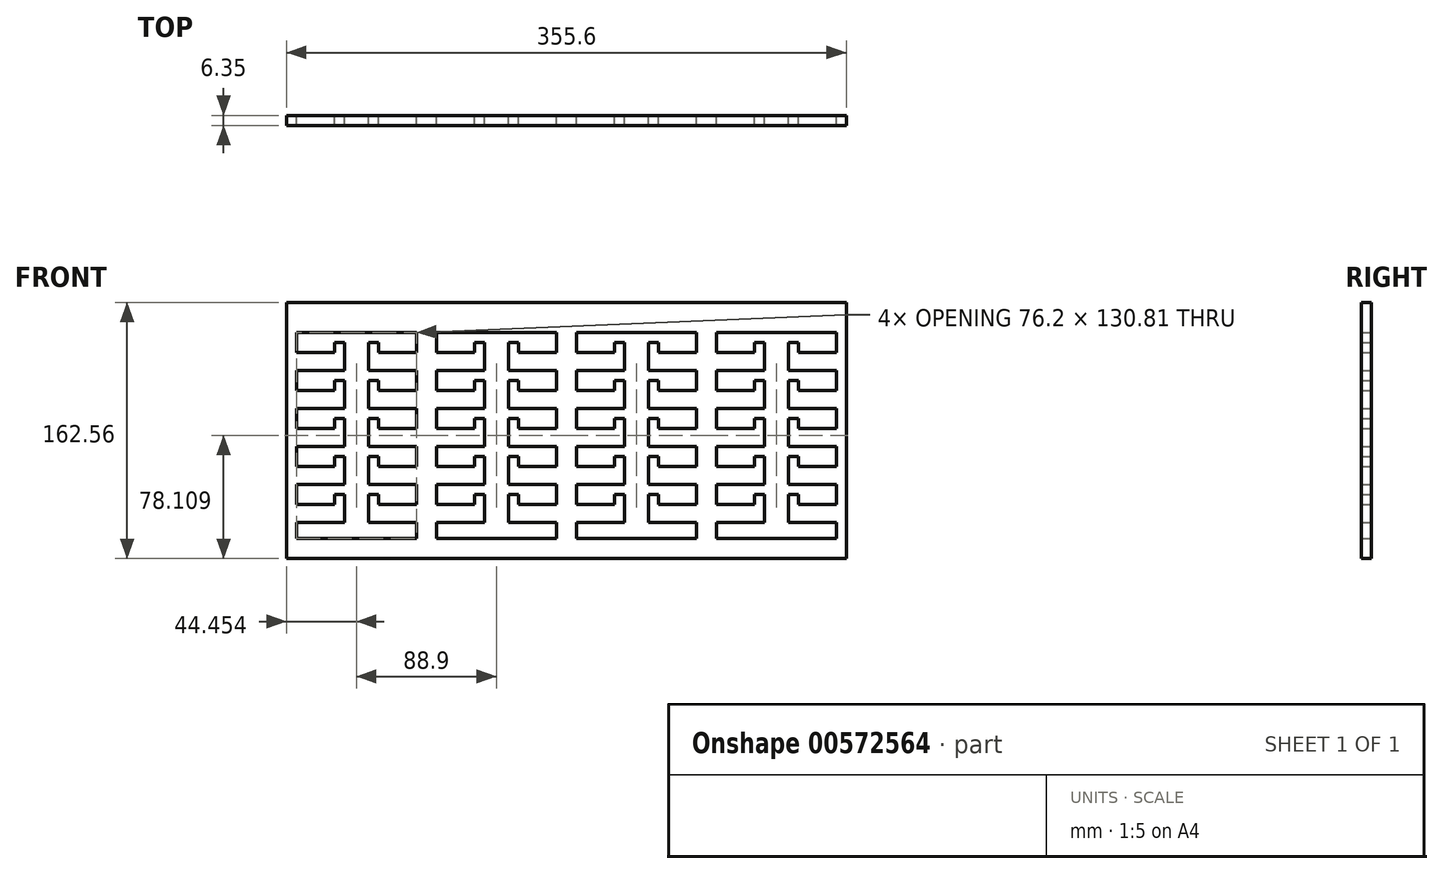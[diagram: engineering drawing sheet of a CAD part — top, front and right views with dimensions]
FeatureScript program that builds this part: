
annotation { "Feature Type Name" : "Feature", "Feature Type Description" : "" }
export const myFeature = defineFeature(function(context is Context, id is Id, definition is map)
    precondition{}
    {
        {
            var Q0;
            Q0=qCreatedBy(makeId("Front.planeOp"),FACE);
            var sketch = newSketch(context, id + "F0", { "sketchPlane" : qUnion([Q0])});
            skLineSegment(sketch, "E0", {"start": v(-96.23, -25.4) * mm, "end": v(-65.75, -25.4) * mm});
            skLineSegment(sketch, "E1", {"start": v(-65.75, -25.4) * mm, "end": v(-65.75, -7.62) * mm});
            skLineSegment(sketch, "E2", {"start": v(-65.75, -7.62) * mm, "end": v(-72.1, -7.62) * mm});
            skLineSegment(sketch, "E3", {"start": v(-72.1, -7.62) * mm, "end": v(-72.1, -13.97) * mm});
            skLineSegment(sketch, "E4", {"start": v(-72.1, -13.97) * mm, "end": v(-96.23, -13.97) * mm});
            skLineSegment(sketch, "E5", {"start": v(-96.23, -13.97) * mm, "end": v(-96.23, -1.27) * mm});
            skLineSegment(sketch, "E6", {"start": v(-96.23, -1.27) * mm, "end": v(-65.75, -1.27) * mm});
            skLineSegment(sketch, "E7", {"start": v(-65.75, -1.27) * mm, "end": v(-65.75, 16.51) * mm});
            skLineSegment(sketch, "E8", {"start": v(-65.75, 16.51) * mm, "end": v(-72.1, 16.51) * mm});
            skLineSegment(sketch, "E9", {"start": v(-72.1, 16.51) * mm, "end": v(-72.1, 10.16) * mm});
            skLineSegment(sketch, "E10", {"start": v(-72.1, 10.16) * mm, "end": v(-96.23, 10.16) * mm});
            skLineSegment(sketch, "E11", {"start": v(-96.23, 10.16) * mm, "end": v(-96.23, 22.86) * mm});
            skLineSegment(sketch, "E12", {"start": v(-96.23, 22.86) * mm, "end": v(-65.75, 22.86) * mm});
            skLineSegment(sketch, "E13", {"start": v(-65.75, 22.86) * mm, "end": v(-65.75, 40.64) * mm});
            skLineSegment(sketch, "E14", {"start": v(-65.75, 40.64) * mm, "end": v(-72.1, 40.64) * mm});
            skLineSegment(sketch, "E15", {"start": v(-72.1, 40.64) * mm, "end": v(-72.1, 34.3) * mm});
            skLineSegment(sketch, "E16", {"start": v(-72.1, 34.3) * mm, "end": v(-96.23, 34.3) * mm});
            skLineSegment(sketch, "E17", {"start": v(-96.23, 34.3) * mm, "end": v(-96.23, 47) * mm});
            skLineSegment(sketch, "E18", {"start": v(-96.23, 47) * mm, "end": v(-65.75, 47) * mm});
            skLineSegment(sketch, "E19", {"start": v(-65.75, 64.77) * mm, "end": v(-72.1, 64.77) * mm});
            skLineSegment(sketch, "E20", {"start": v(-72.1, 64.77) * mm, "end": v(-72.1, 58.42) * mm});
            skLineSegment(sketch, "E21", {"start": v(-72.1, 58.42) * mm, "end": v(-96.23, 58.42) * mm});
            skLineSegment(sketch, "E22", {"start": v(-96.23, 58.42) * mm, "end": v(-96.23, 71.12) * mm});
            skLineSegment(sketch, "E23", {"start": v(-20.03, -59.69) * mm, "end": v(-20.03, -49.53) * mm});
            skLineSegment(sketch, "E24", {"start": v(-20.03, -49.53) * mm, "end": v(-50.5, -49.53) * mm});
            skLineSegment(sketch, "E25", {"start": v(-50.5, -49.53) * mm, "end": v(-50.5, -31.75) * mm});
            skLineSegment(sketch, "E26", {"start": v(-50.5, -31.75) * mm, "end": v(-44.16, -31.75) * mm});
            skLineSegment(sketch, "E27", {"start": v(-44.16, -31.75) * mm, "end": v(-44.16, -38.1) * mm});
            skLineSegment(sketch, "E28", {"start": v(-44.16, -38.1) * mm, "end": v(-20.03, -38.1) * mm});
            skLineSegment(sketch, "E29", {"start": v(-20.03, -38.1) * mm, "end": v(-20.03, -25.4) * mm});
            skLineSegment(sketch, "E30", {"start": v(-20.03, -25.4) * mm, "end": v(-50.5, -25.4) * mm});
            skLineSegment(sketch, "E31", {"start": v(-50.5, -25.4) * mm, "end": v(-50.5, -7.62) * mm});
            skLineSegment(sketch, "E32", {"start": v(-50.5, -7.62) * mm, "end": v(-44.16, -7.62) * mm});
            skLineSegment(sketch, "E33", {"start": v(-44.16, -7.62) * mm, "end": v(-44.16, -13.97) * mm});
            skLineSegment(sketch, "E34", {"start": v(-44.16, -13.97) * mm, "end": v(-20.03, -13.97) * mm});
            skLineSegment(sketch, "E35", {"start": v(-20.03, -13.97) * mm, "end": v(-20.03, -1.27) * mm});
            skLineSegment(sketch, "E36", {"start": v(-20.03, -1.27) * mm, "end": v(-50.5, -1.27) * mm});
            skLineSegment(sketch, "E37", {"start": v(-50.5, -1.27) * mm, "end": v(-50.5, 16.51) * mm});
            skLineSegment(sketch, "E38", {"start": v(-50.5, 16.51) * mm, "end": v(-44.16, 16.51) * mm});
            skLineSegment(sketch, "E39", {"start": v(-44.16, 16.51) * mm, "end": v(-44.16, 10.16) * mm});
            skLineSegment(sketch, "E40", {"start": v(-44.16, 10.16) * mm, "end": v(-20.03, 10.16) * mm});
            skLineSegment(sketch, "E41", {"start": v(-20.03, 10.16) * mm, "end": v(-20.03, 22.86) * mm});
            skLineSegment(sketch, "E42", {"start": v(-20.03, 22.86) * mm, "end": v(-50.5, 22.86) * mm});
            skLineSegment(sketch, "E43", {"start": v(-50.5, 22.86) * mm, "end": v(-50.5, 40.64) * mm});
            skLineSegment(sketch, "E44", {"start": v(-50.5, 40.64) * mm, "end": v(-44.16, 40.64) * mm});
            skLineSegment(sketch, "E45", {"start": v(-44.16, 40.64) * mm, "end": v(-44.16, 34.3) * mm});
            skLineSegment(sketch, "E46", {"start": v(-44.16, 34.3) * mm, "end": v(-20.03, 34.3) * mm});
            skLineSegment(sketch, "E47", {"start": v(-20.03, 34.3) * mm, "end": v(-20.03, 47) * mm});
            skLineSegment(sketch, "E48", {"start": v(-20.03, 47) * mm, "end": v(-50.5, 47) * mm});
            skLineSegment(sketch, "E49", {"start": v(-50.5, 47) * mm, "end": v(-50.5, 64.77) * mm});
            skLineSegment(sketch, "E50", {"start": v(-50.5, 64.77) * mm, "end": v(-44.16, 64.77) * mm});
            skLineSegment(sketch, "E51", {"start": v(-44.16, 64.77) * mm, "end": v(-44.16, 58.42) * mm});
            skLineSegment(sketch, "E52", {"start": v(-44.16, 58.42) * mm, "end": v(-20.03, 58.42) * mm});
            skLineSegment(sketch, "E53", {"start": v(-20.03, 58.42) * mm, "end": v(-20.03, 71.12) * mm});
            skLineSegment(sketch, "E54", {"start": v(-65.75, 47) * mm, "end": v(-65.75, 64.77) * mm});
            skLineSegment(sketch, "E55", {"start": v(-65.75, -49.53) * mm, "end": v(-65.75, -31.75) * mm});
            skLineSegment(sketch, "E56", {"start": v(-72.1, -38.1) * mm, "end": v(-72.1, -31.75) * mm});
            skLineSegment(sketch, "E57", {"start": v(-72.1, -31.75) * mm, "end": v(-65.75, -31.75) * mm});
            skLineSegment(sketch, "E58", {"start": v(-65.75, -49.53) * mm, "end": v(-96.23, -49.53) * mm});
            skLineSegment(sketch, "E59", {"start": v(-96.23, -38.1) * mm, "end": v(-96.23, -25.4) * mm});
            skLineSegment(sketch, "E60", {"start": v(-96.23, -49.53) * mm, "end": v(-96.23, -59.69) * mm});
            skLineSegment(sketch, "E61", {"start": v(-96.23, -38.1) * mm, "end": v(-72.1, -38.1) * mm});
            skLineSegment(sketch, "E62", {"start": v(-96.23, -59.69) * mm, "end": v(-20.03, -59.69) * mm});
            skLineSegment(sketch, "E63", {"start": v(-96.23, 71.12) * mm, "end": v(-20.03, 71.12) * mm});
            skPoint(sketch, "E64", {"position": v(-58.13, 71.12) * mm});
            skPoint(sketch, "E65", {"position": v(-58.13, -59.69) * mm});
            skLineSegment(sketch, "E66", {"start": v(-185.13, -25.4) * mm, "end": v(-154.65, -25.4) * mm});
            skLineSegment(sketch, "E67", {"start": v(-154.65, -25.4) * mm, "end": v(-154.65, -7.62) * mm});
            skLineSegment(sketch, "E68", {"start": v(-154.65, -7.62) * mm, "end": v(-161, -7.62) * mm});
            skLineSegment(sketch, "E69", {"start": v(-161, -7.62) * mm, "end": v(-161, -13.97) * mm});
            skLineSegment(sketch, "E70", {"start": v(-161, -13.97) * mm, "end": v(-185.13, -13.97) * mm});
            skLineSegment(sketch, "E71", {"start": v(-185.13, -13.97) * mm, "end": v(-185.13, -1.27) * mm});
            skLineSegment(sketch, "E72", {"start": v(-185.13, -1.27) * mm, "end": v(-154.65, -1.27) * mm});
            skLineSegment(sketch, "E73", {"start": v(-154.65, -1.27) * mm, "end": v(-154.65, 16.51) * mm});
            skLineSegment(sketch, "E74", {"start": v(-154.65, 16.51) * mm, "end": v(-161, 16.51) * mm});
            skLineSegment(sketch, "E75", {"start": v(-161, 16.51) * mm, "end": v(-161, 10.16) * mm});
            skLineSegment(sketch, "E76", {"start": v(-161, 10.16) * mm, "end": v(-185.13, 10.16) * mm});
            skLineSegment(sketch, "E77", {"start": v(-185.13, 10.16) * mm, "end": v(-185.13, 22.86) * mm});
            skLineSegment(sketch, "E78", {"start": v(-185.13, 22.86) * mm, "end": v(-154.65, 22.86) * mm});
            skLineSegment(sketch, "E79", {"start": v(-154.65, 22.86) * mm, "end": v(-154.65, 40.64) * mm});
            skLineSegment(sketch, "E80", {"start": v(-154.65, 40.64) * mm, "end": v(-161, 40.64) * mm});
            skLineSegment(sketch, "E81", {"start": v(-161, 40.64) * mm, "end": v(-161, 34.3) * mm});
            skLineSegment(sketch, "E82", {"start": v(-161, 34.3) * mm, "end": v(-185.13, 34.3) * mm});
            skLineSegment(sketch, "E83", {"start": v(-185.13, 34.3) * mm, "end": v(-185.13, 47) * mm});
            skLineSegment(sketch, "E84", {"start": v(-185.13, 47) * mm, "end": v(-154.65, 47) * mm});
            skLineSegment(sketch, "E85", {"start": v(-154.65, 64.77) * mm, "end": v(-161, 64.77) * mm});
            skLineSegment(sketch, "E86", {"start": v(-161, 64.77) * mm, "end": v(-161, 58.42) * mm});
            skLineSegment(sketch, "E87", {"start": v(-161, 58.42) * mm, "end": v(-185.13, 58.42) * mm});
            skLineSegment(sketch, "E88", {"start": v(-185.13, 58.42) * mm, "end": v(-185.13, 71.12) * mm});
            skLineSegment(sketch, "E89", {"start": v(-108.93, -59.69) * mm, "end": v(-108.93, -49.53) * mm});
            skLineSegment(sketch, "E90", {"start": v(-108.93, -49.53) * mm, "end": v(-139.4, -49.53) * mm});
            skLineSegment(sketch, "E91", {"start": v(-139.4, -49.53) * mm, "end": v(-139.4, -31.75) * mm});
            skLineSegment(sketch, "E92", {"start": v(-139.4, -31.75) * mm, "end": v(-133.06, -31.75) * mm});
            skLineSegment(sketch, "E93", {"start": v(-133.06, -31.75) * mm, "end": v(-133.06, -38.1) * mm});
            skLineSegment(sketch, "E94", {"start": v(-133.06, -38.1) * mm, "end": v(-108.93, -38.1) * mm});
            skLineSegment(sketch, "E95", {"start": v(-108.93, -38.1) * mm, "end": v(-108.93, -25.4) * mm});
            skLineSegment(sketch, "E96", {"start": v(-108.93, -25.4) * mm, "end": v(-139.4, -25.4) * mm});
            skLineSegment(sketch, "E97", {"start": v(-139.4, -25.4) * mm, "end": v(-139.4, -7.62) * mm});
            skLineSegment(sketch, "E98", {"start": v(-139.4, -7.62) * mm, "end": v(-133.06, -7.62) * mm});
            skLineSegment(sketch, "E99", {"start": v(-133.06, -7.62) * mm, "end": v(-133.06, -13.97) * mm});
            skLineSegment(sketch, "E100", {"start": v(-133.06, -13.97) * mm, "end": v(-108.93, -13.97) * mm});
            skLineSegment(sketch, "E101", {"start": v(-108.93, -13.97) * mm, "end": v(-108.93, -1.27) * mm});
            skLineSegment(sketch, "E102", {"start": v(-108.93, -1.27) * mm, "end": v(-139.4, -1.27) * mm});
            skLineSegment(sketch, "E103", {"start": v(-139.4, -1.27) * mm, "end": v(-139.4, 16.51) * mm});
            skLineSegment(sketch, "E104", {"start": v(-139.4, 16.51) * mm, "end": v(-133.06, 16.51) * mm});
            skLineSegment(sketch, "E105", {"start": v(-133.06, 16.51) * mm, "end": v(-133.06, 10.16) * mm});
            skLineSegment(sketch, "E106", {"start": v(-133.06, 10.16) * mm, "end": v(-108.93, 10.16) * mm});
            skLineSegment(sketch, "E107", {"start": v(-108.93, 10.16) * mm, "end": v(-108.93, 22.86) * mm});
            skLineSegment(sketch, "E108", {"start": v(-108.93, 22.86) * mm, "end": v(-139.4, 22.86) * mm});
            skLineSegment(sketch, "E109", {"start": v(-139.4, 22.86) * mm, "end": v(-139.4, 40.64) * mm});
            skLineSegment(sketch, "E110", {"start": v(-139.4, 40.64) * mm, "end": v(-133.06, 40.64) * mm});
            skLineSegment(sketch, "E111", {"start": v(-133.06, 40.64) * mm, "end": v(-133.06, 34.3) * mm});
            skLineSegment(sketch, "E112", {"start": v(-133.06, 34.3) * mm, "end": v(-108.93, 34.3) * mm});
            skLineSegment(sketch, "E113", {"start": v(-108.93, 34.3) * mm, "end": v(-108.93, 47) * mm});
            skLineSegment(sketch, "E114", {"start": v(-108.93, 47) * mm, "end": v(-139.4, 47) * mm});
            skLineSegment(sketch, "E115", {"start": v(-139.4, 47) * mm, "end": v(-139.4, 64.77) * mm});
            skLineSegment(sketch, "E116", {"start": v(-139.4, 64.77) * mm, "end": v(-133.06, 64.77) * mm});
            skLineSegment(sketch, "E117", {"start": v(-133.06, 64.77) * mm, "end": v(-133.06, 58.42) * mm});
            skLineSegment(sketch, "E118", {"start": v(-133.06, 58.42) * mm, "end": v(-108.93, 58.42) * mm});
            skLineSegment(sketch, "E119", {"start": v(-108.93, 58.42) * mm, "end": v(-108.93, 71.12) * mm});
            skLineSegment(sketch, "E120", {"start": v(-154.65, 47) * mm, "end": v(-154.65, 64.77) * mm});
            skLineSegment(sketch, "E121", {"start": v(-154.65, -49.53) * mm, "end": v(-154.65, -31.75) * mm});
            skLineSegment(sketch, "E122", {"start": v(-161, -38.1) * mm, "end": v(-161, -31.75) * mm});
            skLineSegment(sketch, "E123", {"start": v(-161, -31.75) * mm, "end": v(-154.65, -31.75) * mm});
            skLineSegment(sketch, "E124", {"start": v(-154.65, -49.53) * mm, "end": v(-185.13, -49.53) * mm});
            skLineSegment(sketch, "E125", {"start": v(-185.13, -38.1) * mm, "end": v(-185.13, -25.4) * mm});
            skLineSegment(sketch, "E126", {"start": v(-185.13, -49.53) * mm, "end": v(-185.13, -59.69) * mm});
            skLineSegment(sketch, "E127", {"start": v(-185.13, -38.1) * mm, "end": v(-161, -38.1) * mm});
            skLineSegment(sketch, "E128", {"start": v(-185.13, -59.69) * mm, "end": v(-108.93, -59.69) * mm});
            skLineSegment(sketch, "E129", {"start": v(-185.13, 71.12) * mm, "end": v(-108.93, 71.12) * mm});
            skPoint(sketch, "E130", {"position": v(-147.03, 71.12) * mm});
            skPoint(sketch, "E131", {"position": v(-147.03, -59.69) * mm});
            skLineSegment(sketch, "E132", {"start": v(-274.03, -25.4) * mm, "end": v(-243.55, -25.4) * mm});
            skLineSegment(sketch, "E133", {"start": v(-243.55, -25.4) * mm, "end": v(-243.55, -7.62) * mm});
            skLineSegment(sketch, "E134", {"start": v(-243.55, -7.62) * mm, "end": v(-249.9, -7.62) * mm});
            skLineSegment(sketch, "E135", {"start": v(-249.9, -7.62) * mm, "end": v(-249.9, -13.97) * mm});
            skLineSegment(sketch, "E136", {"start": v(-249.9, -13.97) * mm, "end": v(-274.03, -13.97) * mm});
            skLineSegment(sketch, "E137", {"start": v(-274.03, -13.97) * mm, "end": v(-274.03, -1.27) * mm});
            skLineSegment(sketch, "E138", {"start": v(-274.03, -1.27) * mm, "end": v(-243.55, -1.27) * mm});
            skLineSegment(sketch, "E139", {"start": v(-243.55, -1.27) * mm, "end": v(-243.55, 16.51) * mm});
            skLineSegment(sketch, "E140", {"start": v(-243.55, 16.51) * mm, "end": v(-249.9, 16.51) * mm});
            skLineSegment(sketch, "E141", {"start": v(-249.9, 16.51) * mm, "end": v(-249.9, 10.16) * mm});
            skLineSegment(sketch, "E142", {"start": v(-249.9, 10.16) * mm, "end": v(-274.03, 10.16) * mm});
            skLineSegment(sketch, "E143", {"start": v(-274.03, 10.16) * mm, "end": v(-274.03, 22.86) * mm});
            skLineSegment(sketch, "E144", {"start": v(-274.03, 22.86) * mm, "end": v(-243.55, 22.86) * mm});
            skLineSegment(sketch, "E145", {"start": v(-243.55, 22.86) * mm, "end": v(-243.55, 40.64) * mm});
            skLineSegment(sketch, "E146", {"start": v(-243.55, 40.64) * mm, "end": v(-249.9, 40.64) * mm});
            skLineSegment(sketch, "E147", {"start": v(-249.9, 40.64) * mm, "end": v(-249.9, 34.3) * mm});
            skLineSegment(sketch, "E148", {"start": v(-249.9, 34.3) * mm, "end": v(-274.03, 34.3) * mm});
            skLineSegment(sketch, "E149", {"start": v(-274.03, 34.3) * mm, "end": v(-274.03, 47) * mm});
            skLineSegment(sketch, "E150", {"start": v(-274.03, 47) * mm, "end": v(-243.55, 47) * mm});
            skLineSegment(sketch, "E151", {"start": v(-243.55, 64.77) * mm, "end": v(-249.9, 64.77) * mm});
            skLineSegment(sketch, "E152", {"start": v(-249.9, 64.77) * mm, "end": v(-249.9, 58.42) * mm});
            skLineSegment(sketch, "E153", {"start": v(-249.9, 58.42) * mm, "end": v(-274.03, 58.42) * mm});
            skLineSegment(sketch, "E154", {"start": v(-274.03, 58.42) * mm, "end": v(-274.03, 71.12) * mm});
            skLineSegment(sketch, "E155", {"start": v(-197.83, -59.69) * mm, "end": v(-197.83, -49.53) * mm});
            skLineSegment(sketch, "E156", {"start": v(-197.83, -49.53) * mm, "end": v(-228.3, -49.53) * mm});
            skLineSegment(sketch, "E157", {"start": v(-228.3, -49.53) * mm, "end": v(-228.3, -31.75) * mm});
            skLineSegment(sketch, "E158", {"start": v(-228.3, -31.75) * mm, "end": v(-221.96, -31.75) * mm});
            skLineSegment(sketch, "E159", {"start": v(-221.96, -31.75) * mm, "end": v(-221.96, -38.1) * mm});
            skLineSegment(sketch, "E160", {"start": v(-221.96, -38.1) * mm, "end": v(-197.83, -38.1) * mm});
            skLineSegment(sketch, "E161", {"start": v(-197.83, -38.1) * mm, "end": v(-197.83, -25.4) * mm});
            skLineSegment(sketch, "E162", {"start": v(-197.83, -25.4) * mm, "end": v(-228.3, -25.4) * mm});
            skLineSegment(sketch, "E163", {"start": v(-228.3, -25.4) * mm, "end": v(-228.3, -7.62) * mm});
            skLineSegment(sketch, "E164", {"start": v(-228.3, -7.62) * mm, "end": v(-221.96, -7.62) * mm});
            skLineSegment(sketch, "E165", {"start": v(-221.96, -7.62) * mm, "end": v(-221.96, -13.97) * mm});
            skLineSegment(sketch, "E166", {"start": v(-221.96, -13.97) * mm, "end": v(-197.83, -13.97) * mm});
            skLineSegment(sketch, "E167", {"start": v(-197.83, -13.97) * mm, "end": v(-197.83, -1.27) * mm});
            skLineSegment(sketch, "E168", {"start": v(-197.83, -1.27) * mm, "end": v(-228.3, -1.27) * mm});
            skLineSegment(sketch, "E169", {"start": v(-228.3, -1.27) * mm, "end": v(-228.3, 16.51) * mm});
            skLineSegment(sketch, "E170", {"start": v(-228.3, 16.51) * mm, "end": v(-221.96, 16.51) * mm});
            skLineSegment(sketch, "E171", {"start": v(-221.96, 16.51) * mm, "end": v(-221.96, 10.16) * mm});
            skLineSegment(sketch, "E172", {"start": v(-221.96, 10.16) * mm, "end": v(-197.83, 10.16) * mm});
            skLineSegment(sketch, "E173", {"start": v(-197.83, 10.16) * mm, "end": v(-197.83, 22.86) * mm});
            skLineSegment(sketch, "E174", {"start": v(-197.83, 22.86) * mm, "end": v(-228.3, 22.86) * mm});
            skLineSegment(sketch, "E175", {"start": v(-228.3, 22.86) * mm, "end": v(-228.3, 40.64) * mm});
            skLineSegment(sketch, "E176", {"start": v(-228.3, 40.64) * mm, "end": v(-221.96, 40.64) * mm});
            skLineSegment(sketch, "E177", {"start": v(-221.96, 40.64) * mm, "end": v(-221.96, 34.3) * mm});
            skLineSegment(sketch, "E178", {"start": v(-221.96, 34.3) * mm, "end": v(-197.83, 34.3) * mm});
            skLineSegment(sketch, "E179", {"start": v(-197.83, 34.3) * mm, "end": v(-197.83, 47) * mm});
            skLineSegment(sketch, "E180", {"start": v(-197.83, 47) * mm, "end": v(-228.3, 47) * mm});
            skLineSegment(sketch, "E181", {"start": v(-228.3, 47) * mm, "end": v(-228.3, 64.77) * mm});
            skLineSegment(sketch, "E182", {"start": v(-228.3, 64.77) * mm, "end": v(-221.96, 64.77) * mm});
            skLineSegment(sketch, "E183", {"start": v(-221.96, 64.77) * mm, "end": v(-221.96, 58.42) * mm});
            skLineSegment(sketch, "E184", {"start": v(-221.96, 58.42) * mm, "end": v(-197.83, 58.42) * mm});
            skLineSegment(sketch, "E185", {"start": v(-197.83, 58.42) * mm, "end": v(-197.83, 71.12) * mm});
            skLineSegment(sketch, "E186", {"start": v(-243.55, 47) * mm, "end": v(-243.55, 64.77) * mm});
            skLineSegment(sketch, "E187", {"start": v(-243.55, -49.53) * mm, "end": v(-243.55, -31.75) * mm});
            skLineSegment(sketch, "E188", {"start": v(-249.9, -38.1) * mm, "end": v(-249.9, -31.75) * mm});
            skLineSegment(sketch, "E189", {"start": v(-249.9, -31.75) * mm, "end": v(-243.55, -31.75) * mm});
            skLineSegment(sketch, "E190", {"start": v(-243.55, -49.53) * mm, "end": v(-274.03, -49.53) * mm});
            skLineSegment(sketch, "E191", {"start": v(-274.03, -38.1) * mm, "end": v(-274.03, -25.4) * mm});
            skLineSegment(sketch, "E192", {"start": v(-274.03, -49.53) * mm, "end": v(-274.03, -59.69) * mm});
            skLineSegment(sketch, "E193", {"start": v(-274.03, -38.1) * mm, "end": v(-249.9, -38.1) * mm});
            skLineSegment(sketch, "E194", {"start": v(-274.03, -59.69) * mm, "end": v(-197.83, -59.69) * mm});
            skLineSegment(sketch, "E195", {"start": v(-274.03, 71.12) * mm, "end": v(-197.83, 71.12) * mm});
            skPoint(sketch, "E196", {"position": v(-235.93, 71.12) * mm});
            skPoint(sketch, "E197", {"position": v(-235.93, -59.69) * mm});
            skLineSegment(sketch, "E198", {"start": v(-362.93, -25.4) * mm, "end": v(-332.45, -25.4) * mm});
            skLineSegment(sketch, "E199", {"start": v(-332.45, -25.4) * mm, "end": v(-332.45, -7.62) * mm});
            skLineSegment(sketch, "E200", {"start": v(-332.45, -7.62) * mm, "end": v(-338.8, -7.62) * mm});
            skLineSegment(sketch, "E201", {"start": v(-338.8, -7.62) * mm, "end": v(-338.8, -13.97) * mm});
            skLineSegment(sketch, "E202", {"start": v(-338.8, -13.97) * mm, "end": v(-362.93, -13.97) * mm});
            skLineSegment(sketch, "E203", {"start": v(-362.93, -13.97) * mm, "end": v(-362.93, -1.27) * mm});
            skLineSegment(sketch, "E204", {"start": v(-362.93, -1.27) * mm, "end": v(-332.45, -1.27) * mm});
            skLineSegment(sketch, "E205", {"start": v(-332.45, -1.27) * mm, "end": v(-332.45, 16.51) * mm});
            skLineSegment(sketch, "E206", {"start": v(-332.45, 16.51) * mm, "end": v(-338.8, 16.51) * mm});
            skLineSegment(sketch, "E207", {"start": v(-338.8, 16.51) * mm, "end": v(-338.8, 10.16) * mm});
            skLineSegment(sketch, "E208", {"start": v(-338.8, 10.16) * mm, "end": v(-362.93, 10.16) * mm});
            skLineSegment(sketch, "E209", {"start": v(-362.93, 10.16) * mm, "end": v(-362.93, 22.86) * mm});
            skLineSegment(sketch, "E210", {"start": v(-362.93, 22.86) * mm, "end": v(-332.45, 22.86) * mm});
            skLineSegment(sketch, "E211", {"start": v(-332.45, 22.86) * mm, "end": v(-332.45, 40.64) * mm});
            skLineSegment(sketch, "E212", {"start": v(-332.45, 40.64) * mm, "end": v(-338.8, 40.64) * mm});
            skLineSegment(sketch, "E213", {"start": v(-338.8, 40.64) * mm, "end": v(-338.8, 34.3) * mm});
            skLineSegment(sketch, "E214", {"start": v(-338.8, 34.3) * mm, "end": v(-362.93, 34.3) * mm});
            skLineSegment(sketch, "E215", {"start": v(-362.93, 34.3) * mm, "end": v(-362.93, 47) * mm});
            skLineSegment(sketch, "E216", {"start": v(-362.93, 47) * mm, "end": v(-332.45, 47) * mm});
            skLineSegment(sketch, "E217", {"start": v(-332.45, 64.77) * mm, "end": v(-338.8, 64.77) * mm});
            skLineSegment(sketch, "E218", {"start": v(-338.8, 64.77) * mm, "end": v(-338.8, 58.42) * mm});
            skLineSegment(sketch, "E219", {"start": v(-338.8, 58.42) * mm, "end": v(-362.93, 58.42) * mm});
            skLineSegment(sketch, "E220", {"start": v(-362.93, 58.42) * mm, "end": v(-362.93, 71.12) * mm});
            skLineSegment(sketch, "E221", {"start": v(-286.73, -59.69) * mm, "end": v(-286.73, -49.53) * mm});
            skLineSegment(sketch, "E222", {"start": v(-286.73, -49.53) * mm, "end": v(-317.2, -49.53) * mm});
            skLineSegment(sketch, "E223", {"start": v(-317.2, -49.53) * mm, "end": v(-317.2, -31.75) * mm});
            skLineSegment(sketch, "E224", {"start": v(-317.2, -31.75) * mm, "end": v(-310.86, -31.75) * mm});
            skLineSegment(sketch, "E225", {"start": v(-310.86, -31.75) * mm, "end": v(-310.86, -38.1) * mm});
            skLineSegment(sketch, "E226", {"start": v(-310.86, -38.1) * mm, "end": v(-286.73, -38.1) * mm});
            skLineSegment(sketch, "E227", {"start": v(-286.73, -38.1) * mm, "end": v(-286.73, -25.4) * mm});
            skLineSegment(sketch, "E228", {"start": v(-286.73, -25.4) * mm, "end": v(-317.2, -25.4) * mm});
            skLineSegment(sketch, "E229", {"start": v(-317.2, -25.4) * mm, "end": v(-317.2, -7.62) * mm});
            skLineSegment(sketch, "E230", {"start": v(-317.2, -7.62) * mm, "end": v(-310.86, -7.62) * mm});
            skLineSegment(sketch, "E231", {"start": v(-310.86, -7.62) * mm, "end": v(-310.86, -13.97) * mm});
            skLineSegment(sketch, "E232", {"start": v(-310.86, -13.97) * mm, "end": v(-286.73, -13.97) * mm});
            skLineSegment(sketch, "E233", {"start": v(-286.73, -13.97) * mm, "end": v(-286.73, -1.27) * mm});
            skLineSegment(sketch, "E234", {"start": v(-286.73, -1.27) * mm, "end": v(-317.2, -1.27) * mm});
            skLineSegment(sketch, "E235", {"start": v(-317.2, -1.27) * mm, "end": v(-317.2, 16.51) * mm});
            skLineSegment(sketch, "E236", {"start": v(-317.2, 16.51) * mm, "end": v(-310.86, 16.51) * mm});
            skLineSegment(sketch, "E237", {"start": v(-310.86, 16.51) * mm, "end": v(-310.86, 10.16) * mm});
            skLineSegment(sketch, "E238", {"start": v(-310.86, 10.16) * mm, "end": v(-286.73, 10.16) * mm});
            skLineSegment(sketch, "E239", {"start": v(-286.73, 10.16) * mm, "end": v(-286.73, 22.86) * mm});
            skLineSegment(sketch, "E240", {"start": v(-286.73, 22.86) * mm, "end": v(-317.2, 22.86) * mm});
            skLineSegment(sketch, "E241", {"start": v(-317.2, 22.86) * mm, "end": v(-317.2, 40.64) * mm});
            skLineSegment(sketch, "E242", {"start": v(-317.2, 40.64) * mm, "end": v(-310.86, 40.64) * mm});
            skLineSegment(sketch, "E243", {"start": v(-310.86, 40.64) * mm, "end": v(-310.86, 34.3) * mm});
            skLineSegment(sketch, "E244", {"start": v(-310.86, 34.3) * mm, "end": v(-286.73, 34.3) * mm});
            skLineSegment(sketch, "E245", {"start": v(-286.73, 34.3) * mm, "end": v(-286.73, 47) * mm});
            skLineSegment(sketch, "E246", {"start": v(-286.73, 47) * mm, "end": v(-317.2, 47) * mm});
            skLineSegment(sketch, "E247", {"start": v(-317.2, 47) * mm, "end": v(-317.2, 64.77) * mm});
            skLineSegment(sketch, "E248", {"start": v(-317.2, 64.77) * mm, "end": v(-310.86, 64.77) * mm});
            skLineSegment(sketch, "E249", {"start": v(-310.86, 64.77) * mm, "end": v(-310.86, 58.42) * mm});
            skLineSegment(sketch, "E250", {"start": v(-310.86, 58.42) * mm, "end": v(-286.73, 58.42) * mm});
            skLineSegment(sketch, "E251", {"start": v(-286.73, 58.42) * mm, "end": v(-286.73, 71.12) * mm});
            skLineSegment(sketch, "E252", {"start": v(-332.45, 47) * mm, "end": v(-332.45, 64.77) * mm});
            skLineSegment(sketch, "E253", {"start": v(-332.45, -49.53) * mm, "end": v(-332.45, -31.75) * mm});
            skLineSegment(sketch, "E254", {"start": v(-338.8, -38.1) * mm, "end": v(-338.8, -31.75) * mm});
            skLineSegment(sketch, "E255", {"start": v(-338.8, -31.75) * mm, "end": v(-332.45, -31.75) * mm});
            skLineSegment(sketch, "E256", {"start": v(-332.45, -49.53) * mm, "end": v(-362.93, -49.53) * mm});
            skLineSegment(sketch, "E257", {"start": v(-362.93, -38.1) * mm, "end": v(-362.93, -25.4) * mm});
            skLineSegment(sketch, "E258", {"start": v(-362.93, -49.53) * mm, "end": v(-362.93, -59.69) * mm});
            skLineSegment(sketch, "E259", {"start": v(-362.93, -38.1) * mm, "end": v(-338.8, -38.1) * mm});
            skLineSegment(sketch, "E260", {"start": v(-362.93, -59.69) * mm, "end": v(-286.73, -59.69) * mm});
            skLineSegment(sketch, "E261", {"start": v(-362.93, 71.12) * mm, "end": v(-286.73, 71.12) * mm});
            skPoint(sketch, "E262", {"position": v(-324.83, 71.12) * mm});
            skPoint(sketch, "E263", {"position": v(-324.83, -59.69) * mm});
            skLineSegment(sketch, "E264.bottom", {"start": v(-13.68, 90.17) * mm, "end": v(-369.28, 90.17) * mm});
            skLineSegment(sketch, "E264.top", {"start": v(-13.68, -72.39) * mm, "end": v(-369.28, -72.39) * mm});
            skLineSegment(sketch, "E264.left", {"start": v(-13.68, 90.17) * mm, "end": v(-13.68, -72.39) * mm});
            skLineSegment(sketch, "E264.right", {"start": v(-369.28, 90.17) * mm, "end": v(-369.28, -72.39) * mm});
            skPoint(sketch, "E265", {"position": v(-191.48, 90.17) * mm});
            skLineSegment(sketch, "E266", {"start": v(-197.83, 71.12) * mm, "end": v(-185.13, 71.12) * mm});
            skPoint(sketch, "E267", {"position": v(-191.48, 71.12) * mm});
            skSolve(sketch);
        }
        {
            var Q0;
            Q0=makeQuery(id+"F0.imprint","IMPRINT",FACE,{"disambiguationData":[TD([[makeQuery(id+"F0.imprint","IMPRINT",EDGE,{"derivedFrom":sQuery(id+"F0.wireOp",EDGE,"E0")}),1.0]])]});
            extrude(context, id + "F1", {"entities" : qUnion([Q0]), "depth" : 6.35 * mm});
        }
    });
